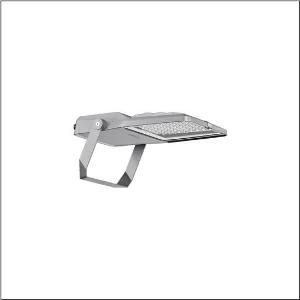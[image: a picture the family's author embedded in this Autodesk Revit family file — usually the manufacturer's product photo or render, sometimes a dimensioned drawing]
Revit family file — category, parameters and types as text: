
# Revit family: floodlight_fl_21_iq_mini___pl43_5xa7772c4a1a_8d49
name_source: partatom
category: Lighting Fixtures
units: mm (PartAtom-declared; Revit-internal decimal feet)

## family parameters
Cut with Voids When Loaded = No
Host = Face
Light Source = No
Part Type = Normal
Room Calculation Point = No
Round Connector Dimension = Use Diameter
Shared = No

## types (1)
- --- (1 x LED, 13050 lm, 87.2 W, 4000K)
    Apparent Load = 87 VA
    CIE Flux Codes = 27 78 99 100 100
    Color Rendering = 70
    Color Temperature = 4000K
    Default Elevation = 1800 mm
    Description = Floodlight FL 21 iQ mini, floodlight, primary light control with lens, of PMMA, primary optical cover: protective disc, of toughened safety glass, transparent, light distribution: PL43, light emission: direct distribution, installation type: surface-mounted, LED, High Power LED, rated luminous flux: 13.050lm, luminous efficacy: 150lm/W, light colour: 740, colour temperature: 4000K, control: Street-Remote, Auto-Match, Temp-Guard, Night-Set, Smart-Wire, Desk-Remote (wireless, voltage-free reading and setting of iQ features in the workshop via application-optimized NFC function/RFID function), optimised constant luminous flux control (CLO 2.0), with terminal, 6-pole, mains connection: 220..240V, AC, 50/60Hz, start of lifetime: 87W, end of service life: 92W, reduction: 40W, luminaire housing, of diecast aluminium, powder-coated, Siteco® metallic grey (DB 702S), corrosivity category C5 mid according to DIN EN ISO 12944, sealing non-destructively replaceable, mounting bracket, of steel, galvanised, powder-coated, Siteco® metallic grey (DB 702S), protection rating (complete): IP66, insulation class (complete): insulation class II (safety insulation), certification: CE, ENEC, VDE, protection symbol: D, impact resistance: IK08, permissible operating ambient temperature: -40..+40°C, permissible operating ambient temperature for outdoor applications: -40..+50°C, standard: DIN EN 12944, LABS conformity tested according to VDMA 24364:2018-05, packaging unit: 1 piece

Light Distribution: PL43
    Height = 70 mm
    Lamp = 1 x LED
    Lamp Light Flux = 13050 lm
    Lamp Power = 87.2 W
    Lamp count = 1
    Length = 485 mm
    Luminous efficacy = 150 lm/W
    Manufacturer = Siteco
    ModVariant = No
    Model = 5XA7772C4A1A
    Number of Poles = 1
    OnlyDefault = Yes
    Power Factor = 1
    Product Name = Floodlight FL 21 iQ mini | PL43
    Product group = floodlight | pylon annexe
    ProductGroupID = 6200
    Protection Class = Protection class II
    Protection Degree = IP 66
    RLX_Detail_Level = 1
    RLX_Emergency_Light_Flux = 0 lm
    RLX_Emergency_Type = 0
    RLX_Emergency_Type_DB = No
    RlxData = <blob elided: 96289 chars, md5=485ebe49>
    Socket = socket
    Standby Power = 0 W
    System Light Flux = 13050 lm
    System Power = 87 W
    Type Comments = factory setting: luminous flux: 100 % | dim-lin: 254 | 456 mA
    Type Image = l_1006845.jpg
    URL = http://relux.com
    VarID = @adj_094129
    Voltage = 0 V
    Weight = 0.00 kg
    Width = 337 mm

## geometry (parser evidence)
native form markers: Blend x4, Sweep x14
no freeform markers — native parametric forms only
